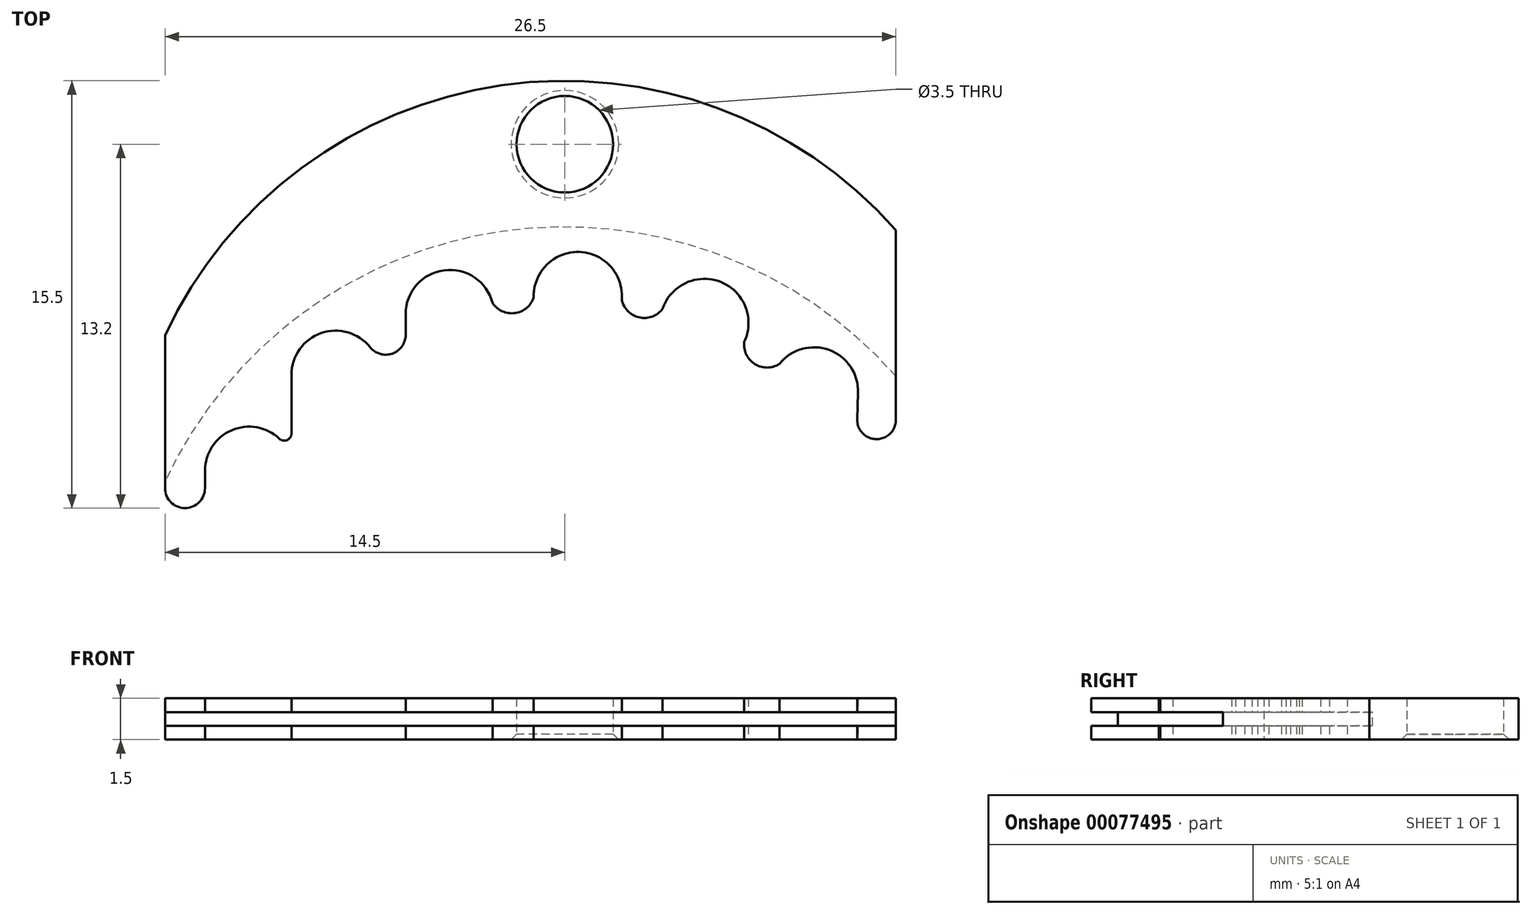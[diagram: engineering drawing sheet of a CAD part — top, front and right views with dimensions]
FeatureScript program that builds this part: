
annotation { "Feature Type Name" : "Feature", "Feature Type Description" : "" }
export const myFeature = defineFeature(function(context is Context, id is Id, definition is map)
    precondition{}
    {
        {
            var Q0;
            Q0=qCreatedBy(makeId("Top.planeOp"),FACE);
            var sketch = newSketch(context, id + "F0", { "sketchPlane" : qUnion([Q0])});
            skCircle(sketch, "E0", {"center": v(0, 0) * mm, "radius": 13 * mm, "construction": true});
            skCircle(sketch, "E1", {"center": v(0, 0) * mm, "radius": 13.5 * mm, "construction": true});
            skCircle(sketch, "E2", {"center": v(0, 0) * mm, "radius": 16 * mm, "construction": true});
            skLineSegment(sketch, "E3", {"start": v(0, 0) * mm, "end": v(0.47, 13.5) * mm, "construction": true});
            skLineSegment(sketch, "E4", {"start": v(0, 0) * mm, "end": v(5.06, 12.52) * mm, "construction": true});
            skLineSegment(sketch, "E5", {"start": v(0, 0) * mm, "end": v(9.03, 10.03) * mm, "construction": true});
            skLineSegment(sketch, "E6", {"start": v(0, 0) * mm, "end": v(-4.17, 12.84) * mm, "construction": true});
            skLineSegment(sketch, "E7", {"start": v(0, 0) * mm, "end": v(-8.31, 10.64) * mm, "construction": true});
            skLineSegment(sketch, "E8", {"start": v(0, 0) * mm, "end": v(-11.45, 7.15) * mm, "construction": true});
            skArc(sketch, "E9", {"start": v(2.06, 13.34) * mm, "mid": v(0.53, 15.1) * mm, "end": v(-1.13, 13.45) * mm});
            skArc(sketch, "E10", {"start": v(6.5, 11.83) * mm, "mid": v(5.66, 14) * mm, "end": v(3.54, 13.03) * mm});
            skArc(sketch, "E11", {"start": v(10.63, 9.98) * mm, "mid": v(9.59, 11.53) * mm, "end": v(7.78, 11.03) * mm});
            skArc(sketch, "E12", {"start": v(-2.62, 13.24) * mm, "mid": v(-4.38, 14.43) * mm, "end": v(-5.77, 12.84) * mm});
            skArc(sketch, "E13", {"start": v(-7, 11.55) * mm, "mid": v(-8.79, 12.17) * mm, "end": v(-9.91, 10.64) * mm});
            skArc(sketch, "E14", {"start": v(-10.35, 8.32) * mm, "mid": v(-12.08, 8.62) * mm, "end": v(-13.05, 7.15) * mm});
            skArc(sketch, "E15", {"start": v(-2.62, 13.24) * mm, "mid": v(-1.8, 12.87) * mm, "end": v(-1.13, 13.45) * mm});
            skArc(sketch, "E16", {"start": v(2.06, 13.34) * mm, "mid": v(2.7, 12.72) * mm, "end": v(3.54, 13.03) * mm});
            skArc(sketch, "E17", {"start": v(6.5, 11.83) * mm, "mid": v(6.89, 11.02) * mm, "end": v(7.78, 11.03) * mm});
            skLineSegment(sketch, "E18", {"start": v(-5.77, 12.84) * mm, "end": v(-5.77, 12.09) * mm});
            skLineSegment(sketch, "E19", {"start": v(-7.06, 11.64) * mm, "end": v(-7.06, 11.64) * mm});
            skArc(sketch, "E20", {"start": v(-7.06, 11.64) * mm, "mid": v(-6.26, 11.4) * mm, "end": v(-5.77, 12.09) * mm});
            skLineSegment(sketch, "E21", {"start": v(-9.91, 10.64) * mm, "end": v(-9.91, 8.5) * mm});
            skArc(sketch, "E22", {"start": v(-10.35, 8.32) * mm, "mid": v(-10.07, 8.27) * mm, "end": v(-9.91, 8.5) * mm});
            skArc(sketch, "E23", {"start": v(-14.5, 6.53) * mm, "mid": v(-13.77, 5.8) * mm, "end": v(-13.05, 6.53) * mm});
            skArc(sketch, "E24", {"start": v(10.6, 9.02) * mm, "mid": v(11.29, 8.3) * mm, "end": v(12, 9) * mm});
            skLineSegment(sketch, "E25", {"start": v(-14.5, 0) * mm, "end": v(-14.5, 12.06) * mm});
            skLineSegment(sketch, "E26", {"start": v(12, 0) * mm, "end": v(12, 15.88) * mm});
            skArc(sketch, "E27", {"start": v(12, 15.88) * mm, "mid": v(-2.28, 21.14) * mm, "end": v(-14.5, 12.06) * mm});
            skLineSegment(sketch, "E28", {"start": v(-13.05, 7.15) * mm, "end": v(-13.05, 6.53) * mm});
            skLineSegment(sketch, "E29", {"start": v(-14.5, 19) * mm, "end": v(12, 19) * mm, "construction": true});
            skLineSegment(sketch, "E30", {"start": v(10.63, 9.98) * mm, "end": v(10.6, 9.02) * mm});
            skCircle(sketch, "E31", {"center": v(0, 19) * mm, "radius": 1.75 * mm});
            skSolve(sketch);
        }
        {
            var Q0;
            Q0=makeQuery(id+"F0.imprint","IMPRINT",FACE,{"disambiguationData":[TD([[makeQuery(id+"F0.imprint","IMPRINT",EDGE,{"derivedFrom":sQuery(id+"F0.wireOp",EDGE,"E9")}),-1.0]])]});
            extrude(context, id + "F1", {"entities" : qUnion([Q0]), "depth" : 1.5 * mm, "symmetric" : true});
        }
        {
            var Q0;
            Q0=makeQuery(id+"F1.opExtrude","CAP_EDGE",EDGE,{"disambiguationData":[OSD([sQuery(id+"F0.wireOp",EDGE,"E31")])],"isStart":true});
            chamfer(context, id + "F2", {"entities" : qUnion([Q0]), "width" : 0.2 * mm, "tangentPropagation" : true});
        }
        {
            var Q0;
            Q0=qCreatedBy(makeId("Top.planeOp"),FACE);
            var sketch = newSketch(context, id + "F3", { "sketchPlane" : qUnion([Q0])});
            skCircle(sketch, "E32", {"center": v(0, 0) * mm, "radius": 16 * mm});
            skSolve(sketch);
        }
        {
            var Q0;
            Q0=makeQuery(id+"F3.imprint","IMPRINT",FACE,{"disambiguationData":[TD([[makeQuery(id+"F3.imprint","IMPRINT",EDGE,{"derivedFrom":sQuery(id+"F3.wireOp",EDGE,"E32")}),1.0]])]});
            extrude(context, id + "F4", {"entities" : qUnion([Q0]), "operationType" : NewBodyOperationType.REMOVE, "oppositeDirection" : true, "depth" : 0.5 * mm, "symmetric" : true});
        }
    });
